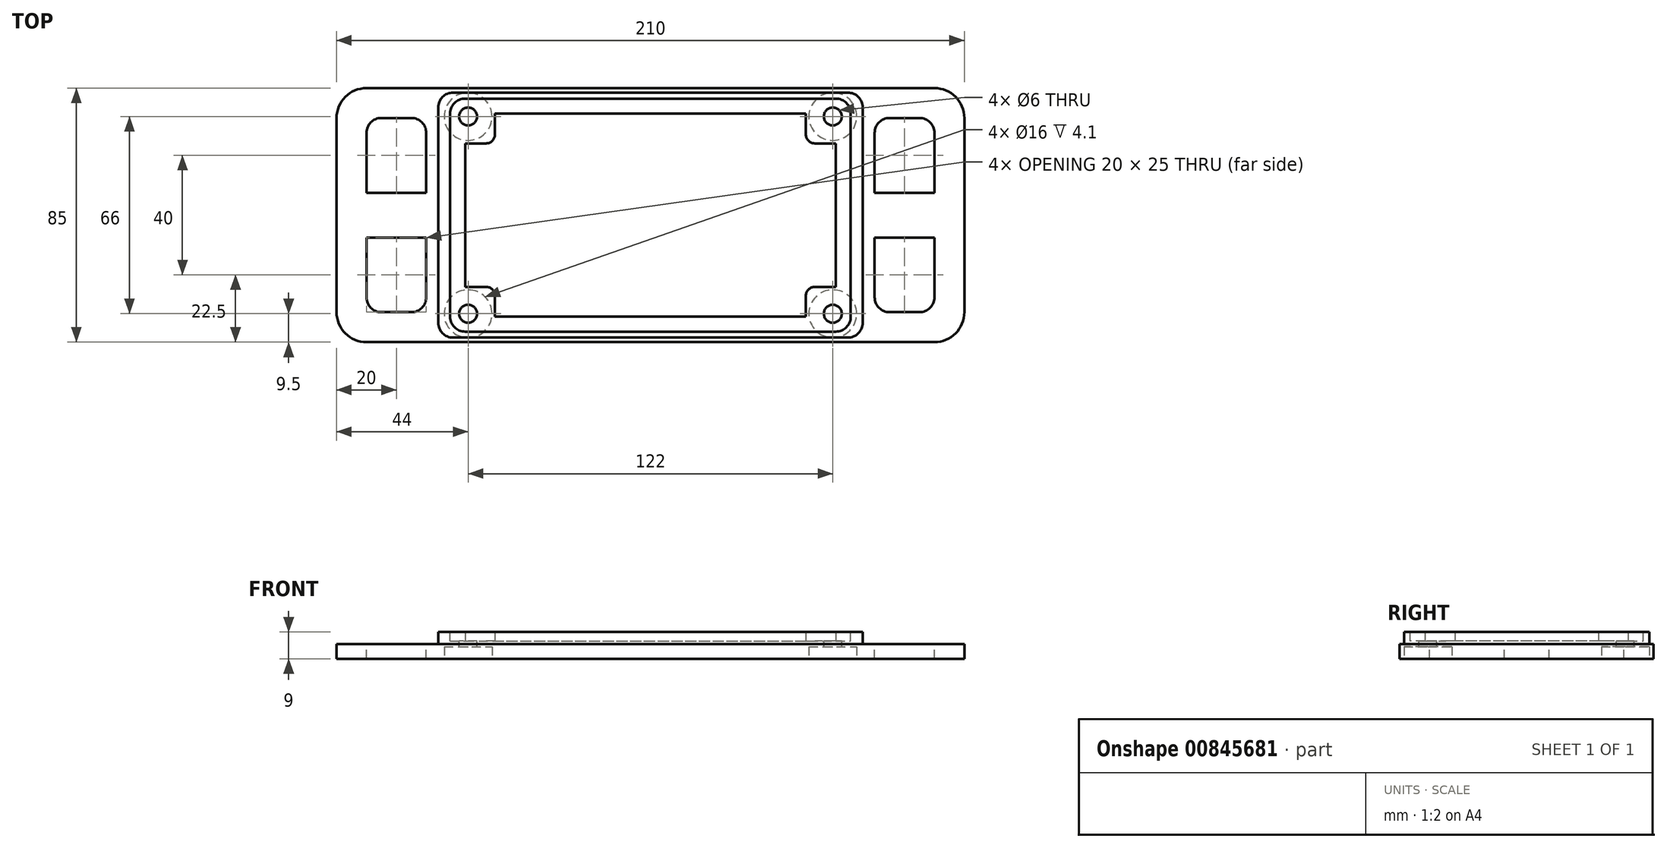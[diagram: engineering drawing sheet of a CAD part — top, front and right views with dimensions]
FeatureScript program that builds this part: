
annotation { "Feature Type Name" : "Feature", "Feature Type Description" : "" }
export const myFeature = defineFeature(function(context is Context, id is Id, definition is map)
    precondition{}
    {
        {
            var Q0;
            Q0=qCreatedBy(makeId("Top.planeOp"),FACE);
            var sketch = newSketch(context, id + "F0", { "sketchPlane" : qUnion([Q0])});
            skLineSegment(sketch, "E0.bottom", {"start": v(-105, 42.5) * mm, "end": v(105, 42.5) * mm});
            skLineSegment(sketch, "E0.top", {"start": v(-105, -42.5) * mm, "end": v(105, -42.5) * mm});
            skLineSegment(sketch, "E0.left", {"start": v(-105, 42.5) * mm, "end": v(-105, -42.5) * mm});
            skLineSegment(sketch, "E0.right", {"start": v(105, 42.5) * mm, "end": v(105, -42.5) * mm});
            skSolve(sketch);
        }
        {
            var Q0;
            Q0 = qSketchRegion(id + "F0", true);
            extrude(context, id + "F1", {"entities" : qUnion([Q0]), "depth" : 5 * mm, "offsetDistance" : 25 * mm});
        }
        {
            var Q0;
            Q0=makeQuery(id+"F1.opExtrude","SWEPT_EDGE",EDGE,{"disambiguationData":[OSD([sQuery(id+"F0.wireOp",EDGE,"E0.top"),sQuery(id+"F0.wireOp",EDGE,"E0.left")])]});
            var Q1;
            Q1=makeQuery(id+"F1.opExtrude","SWEPT_EDGE",EDGE,{"disambiguationData":[OSD([sQuery(id+"F0.wireOp",EDGE,"E0.bottom"),sQuery(id+"F0.wireOp",EDGE,"E0.left")])]});
            var Q2;
            Q2=makeQuery(id+"F1.opExtrude","SWEPT_EDGE",EDGE,{"disambiguationData":[OSD([sQuery(id+"F0.wireOp",EDGE,"E0.bottom"),sQuery(id+"F0.wireOp",EDGE,"E0.right")])]});
            var Q3;
            Q3=makeQuery(id+"F1.opExtrude","SWEPT_EDGE",EDGE,{"disambiguationData":[OSD([sQuery(id+"F0.wireOp",EDGE,"E0.top"),sQuery(id+"F0.wireOp",EDGE,"E0.right")])]});
            fillet(context, id + "F2", {"entities" : qUnion([Q0, Q1, Q2, Q3]), "radius" : 10 * mm, "tangentPropagation" : true, "allowEdgeOverflow" : false});
        }
        {
            var Q0;
            Q0=makeQuery(id+"F1.opExtrude","CAP_FACE",FACE,{"disambiguationData":[OSD([sQuery(id+"F0.wireOp",EDGE,"E0.bottom"),sQuery(id+"F0.wireOp",EDGE,"E0.top"),sQuery(id+"F0.wireOp",EDGE,"E0.left"),sQuery(id+"F0.wireOp",EDGE,"E0.right")])],"isStart":false});
            var sketch = newSketch(context, id + "F3", { "sketchPlane" : qUnion([Q0])});
            skLineSegment(sketch, "E1.bottom", {"start": v(-66, 41) * mm, "end": v(66, 41) * mm});
            skLineSegment(sketch, "E1.top", {"start": v(-66, -41) * mm, "end": v(66, -41) * mm});
            skLineSegment(sketch, "E1.left", {"start": v(-71, 36) * mm, "end": v(-71, -36) * mm});
            skLineSegment(sketch, "E1.right", {"start": v(71, 36) * mm, "end": v(71, -36) * mm});
            skPoint(sketch, "E2.visualSharp", {"position": v(-71, 41) * mm});
            skArc(sketch, "E2.filletArc", {"start": v(-66, 41) * mm, "mid": v(-69.54, 39.54) * mm, "end": v(-71, 36) * mm});
            skPoint(sketch, "E3.visualSharp", {"position": v(-71, -41) * mm});
            skArc(sketch, "E3.filletArc", {"start": v(-71, -36) * mm, "mid": v(-69.54, -39.54) * mm, "end": v(-66, -41) * mm});
            skPoint(sketch, "E4.visualSharp", {"position": v(71, -41) * mm});
            skArc(sketch, "E4.filletArc", {"start": v(66, -41) * mm, "mid": v(69.54, -39.54) * mm, "end": v(71, -36) * mm});
            skPoint(sketch, "E5.visualSharp", {"position": v(71, 41) * mm});
            skArc(sketch, "E5.filletArc", {"start": v(71, 36) * mm, "mid": v(69.54, 39.54) * mm, "end": v(66, 41) * mm});
            skSolve(sketch);
        }
        {
            var Q0;
            Q0 = qSketchRegion(id + "F3", true);
            extrude(context, id + "F4", {"entities" : qUnion([Q0]), "operationType" : NewBodyOperationType.ADD, "depth" : 4 * mm, "offsetDistance" : 25 * mm});
        }
        {
            var Q0;
            Q0=makeQuery(id+"F4.opExtrude","CAP_FACE",FACE,{"disambiguationData":[OSD([sQuery(id+"F3.wireOp",EDGE,"E1.bottom"),sQuery(id+"F3.wireOp",EDGE,"E1.top"),sQuery(id+"F3.wireOp",EDGE,"E1.left"),sQuery(id+"F3.wireOp",EDGE,"E1.right"),sQuery(id+"F3.wireOp",EDGE,"E2.filletArc"),sQuery(id+"F3.wireOp",EDGE,"E3.filletArc"),sQuery(id+"F3.wireOp",EDGE,"E4.filletArc"),sQuery(id+"F3.wireOp",EDGE,"E5.filletArc")])],"isStart":false});
            var sketch = newSketch(context, id + "F5", { "sketchPlane" : qUnion([Q0])});
            skLineSegment(sketch, "E6.bottom", {"start": v(-62, 39) * mm, "end": v(62, 39) * mm});
            skLineSegment(sketch, "E6.top", {"start": v(-62, -39) * mm, "end": v(62, -39) * mm});
            skLineSegment(sketch, "E6.left", {"start": v(-67, 34) * mm, "end": v(-67, -34) * mm});
            skLineSegment(sketch, "E6.right", {"start": v(67, 34) * mm, "end": v(67, -34) * mm});
            skPoint(sketch, "E7.visualSharp", {"position": v(-67, 39) * mm});
            skArc(sketch, "E7.filletArc", {"start": v(-62, 39) * mm, "mid": v(-65.54, 37.54) * mm, "end": v(-67, 34) * mm});
            skPoint(sketch, "E8.visualSharp", {"position": v(-67, -39) * mm});
            skArc(sketch, "E8.filletArc", {"start": v(-67, -34) * mm, "mid": v(-65.54, -37.54) * mm, "end": v(-62, -39) * mm});
            skPoint(sketch, "E9.visualSharp", {"position": v(67, -39) * mm});
            skArc(sketch, "E9.filletArc", {"start": v(62, -39) * mm, "mid": v(65.54, -37.54) * mm, "end": v(67, -34) * mm});
            skPoint(sketch, "E10.visualSharp", {"position": v(67, 39) * mm});
            skArc(sketch, "E10.filletArc", {"start": v(67, 34) * mm, "mid": v(65.54, 37.54) * mm, "end": v(62, 39) * mm});
            skSolve(sketch);
        }
        {
            var Q0;
            Q0 = qSketchRegion(id + "F5", true);
            extrude(context, id + "F6", {"entities" : qUnion([Q0]), "operationType" : NewBodyOperationType.REMOVE, "oppositeDirection" : true, "depth" : 3 * mm, "offsetDistance" : 25 * mm});
        }
        {
            var Q0;
            Q0=makeQuery(id+"F6.boolean.opBoolean","COPY",FACE,{"derivedFrom":makeQuery(id+"F6.opExtrude","CAP_FACE",FACE,{"disambiguationData":[OSD([sQuery(id+"F5.wireOp",EDGE,"E6.bottom"),sQuery(id+"F5.wireOp",EDGE,"E6.top"),sQuery(id+"F5.wireOp",EDGE,"E6.left"),sQuery(id+"F5.wireOp",EDGE,"E6.right"),sQuery(id+"F5.wireOp",EDGE,"E7.filletArc"),sQuery(id+"F5.wireOp",EDGE,"E8.filletArc"),sQuery(id+"F5.wireOp",EDGE,"E9.filletArc"),sQuery(id+"F5.wireOp",EDGE,"E10.filletArc")])],"isStart":false})});
            var sketch = newSketch(context, id + "F7", { "sketchPlane" : qUnion([Q0])});
            skLineSegment(sketch, "E11.bottom", {"start": v(-52, 34) * mm, "end": v(52, 34) * mm});
            skLineSegment(sketch, "E11.top", {"start": v(-52, -34) * mm, "end": v(52, -34) * mm});
            skLineSegment(sketch, "E11.left", {"start": v(-62, 24) * mm, "end": v(-62, -24) * mm});
            skLineSegment(sketch, "E11.right", {"start": v(62, 24) * mm, "end": v(62, -24) * mm});
            skLineSegment(sketch, "E12.top", {"start": v(-62, 24) * mm, "end": v(-55, 24) * mm});
            skLineSegment(sketch, "E12.right", {"start": v(-52, 34) * mm, "end": v(-52, 27) * mm});
            skPoint(sketch, "E13.visualSharp", {"position": v(-52, 24) * mm});
            skArc(sketch, "E13.filletArc", {"start": v(-55, 24) * mm, "mid": v(-52.88, 24.88) * mm, "end": v(-52, 27) * mm});
            skLineSegment(sketch, "E14", {"start": v(0, 19.7) * mm, "end": v(0, -28.15) * mm, "construction": true});
            skLineSegment(sketch, "E15", {"start": v(-18.01, 0) * mm, "end": v(22.05, 0) * mm, "construction": true});
            skLineSegment(sketch, "E16.MirrorCS", {"start": v(-62, -24) * mm, "end": v(-55, -24) * mm});
            skPoint(sketch, "E17.MirrorP", {"position": v(-52, -24) * mm});
            skArc(sketch, "E18.MirrorCS", {"start": v(-55, -24) * mm, "mid": v(-52.88, -24.88) * mm, "end": v(-52, -27) * mm});
            skLineSegment(sketch, "E19.MirrorCS", {"start": v(-52, -34) * mm, "end": v(-52, -27) * mm});
            skLineSegment(sketch, "E20.MirrorCS", {"start": v(62, 24) * mm, "end": v(55, 24) * mm});
            skArc(sketch, "E21.MirrorCS", {"start": v(55, 24) * mm, "mid": v(52.88, 24.88) * mm, "end": v(52, 27) * mm});
            skLineSegment(sketch, "E22.MirrorCS", {"start": v(52, 34) * mm, "end": v(52, 27) * mm});
            skLineSegment(sketch, "E23.MirrorCS", {"start": v(62, -24) * mm, "end": v(55, -24) * mm});
            skLineSegment(sketch, "E24.MirrorCS", {"start": v(52, -34) * mm, "end": v(52, -27) * mm});
            skArc(sketch, "E25.MirrorCS", {"start": v(55, -24) * mm, "mid": v(52.88, -24.88) * mm, "end": v(52, -27) * mm});
            skPoint(sketch, "E26.orphan", {"position": v(-62, 34) * mm});
            skSolve(sketch);
        }
        {
            var Q0;
            Q0 = qSketchRegion(id + "F7", true);
            extrude(context, id + "F8", {"entities" : qUnion([Q0]), "operationType" : NewBodyOperationType.ADD, "depth" : 3 * mm, "offsetDistance" : 25 * mm});
        }
        {
            var Q0;
            Q0=makeQuery(id+"F6.boolean.opBoolean","COPY",FACE,{"derivedFrom":makeQuery(id+"F6.opExtrude","CAP_FACE",FACE,{"disambiguationData":[OSD([sQuery(id+"F5.wireOp",EDGE,"E6.bottom"),sQuery(id+"F5.wireOp",EDGE,"E6.top"),sQuery(id+"F5.wireOp",EDGE,"E6.left"),sQuery(id+"F5.wireOp",EDGE,"E6.right"),sQuery(id+"F5.wireOp",EDGE,"E7.filletArc"),sQuery(id+"F5.wireOp",EDGE,"E8.filletArc"),sQuery(id+"F5.wireOp",EDGE,"E9.filletArc"),sQuery(id+"F5.wireOp",EDGE,"E10.filletArc")])],"isStart":false})});
            var sketch = newSketch(context, id + "F9", { "sketchPlane" : qUnion([Q0])});
            skCircle(sketch, "E27", {"center": v(-61, -33) * mm, "radius": 3 * mm});
            skLineSegment(sketch, "E28", {"start": v(0, 18.3) * mm, "end": v(0, -14.07) * mm, "construction": true});
            skLineSegment(sketch, "E29", {"start": v(-30.9, 0) * mm, "end": v(22.99, 0) * mm, "construction": true});
            skCircle(sketch, "E30.MirrorC", {"center": v(-61, 33) * mm, "radius": 3 * mm});
            skCircle(sketch, "E31.MirrorC", {"center": v(61, -33) * mm, "radius": 3 * mm});
            skCircle(sketch, "E32.MirrorC", {"center": v(61, 33) * mm, "radius": 3 * mm});
            skSolve(sketch);
        }
        {
            var Q0;
            Q0 = qSketchRegion(id + "F9", true);
            extrude(context, id + "F10", {"entities" : qUnion([Q0]), "operationType" : NewBodyOperationType.REMOVE, "oppositeDirection" : true, "depth" : 25 * mm, "offsetDistance" : 25 * mm});
        }
        {
            var Q0;
            Q0=makeQuery(id+"F1.opExtrude","CAP_FACE",FACE,{"disambiguationData":[OSD([sQuery(id+"F0.wireOp",EDGE,"E0.bottom"),sQuery(id+"F0.wireOp",EDGE,"E0.top"),sQuery(id+"F0.wireOp",EDGE,"E0.left"),sQuery(id+"F0.wireOp",EDGE,"E0.right")])],"isStart":true});
            var sketch = newSketch(context, id + "F11", { "sketchPlane" : qUnion([Q0])});
            skCircle(sketch, "E33", {"center": v(-61, 33) * mm, "radius": 8 * mm});
            skCircle(sketch, "E34", {"center": v(-61, -33) * mm, "radius": 8 * mm});
            skCircle(sketch, "E35", {"center": v(61, -33) * mm, "radius": 8 * mm});
            skCircle(sketch, "E36", {"center": v(61, 33) * mm, "radius": 8 * mm});
            skSolve(sketch);
        }
        {
            var Q0;
            Q0 = qSketchRegion(id + "F11", true);
            extrude(context, id + "F12", {"entities" : qUnion([Q0]), "operationType" : NewBodyOperationType.REMOVE, "oppositeDirection" : true, "depth" : 4.1 * mm, "offsetDistance" : 25 * mm});
        }
        {
            var Q0;
            Q0=makeQuery(id+"F1.opExtrude","CAP_FACE",FACE,{"disambiguationData":[OSD([sQuery(id+"F0.wireOp",EDGE,"E0.bottom"),sQuery(id+"F0.wireOp",EDGE,"E0.top"),sQuery(id+"F0.wireOp",EDGE,"E0.left"),sQuery(id+"F0.wireOp",EDGE,"E0.right")])],"isStart":false});
            var sketch = newSketch(context, id + "F13", { "sketchPlane" : qUnion([Q0])});
            skLineSegment(sketch, "E37.bottom", {"start": v(-90, 32.5) * mm, "end": v(-80, 32.5) * mm});
            skLineSegment(sketch, "E37.top", {"start": v(-95, 7.5) * mm, "end": v(-75, 7.5) * mm});
            skLineSegment(sketch, "E37.left", {"start": v(-95, 27.5) * mm, "end": v(-95, 7.5) * mm});
            skLineSegment(sketch, "E37.right", {"start": v(-75, 27.5) * mm, "end": v(-75, 7.5) * mm});
            skLineSegment(sketch, "E38", {"start": v(-27.76, 0) * mm, "end": v(22.14, 0) * mm, "construction": true});
            skLineSegment(sketch, "E39", {"start": v(0, 18.6) * mm, "end": v(0, -20.05) * mm, "construction": true});
            skPoint(sketch, "E40.visualSharp", {"position": v(-95, 32.5) * mm});
            skArc(sketch, "E40.filletArc", {"start": v(-90, 32.5) * mm, "mid": v(-93.54, 31.04) * mm, "end": v(-95, 27.5) * mm});
            skPoint(sketch, "E41.visualSharp", {"position": v(-75, 32.5) * mm});
            skArc(sketch, "E41.filletArc", {"start": v(-75, 27.5) * mm, "mid": v(-76.46, 31.04) * mm, "end": v(-80, 32.5) * mm});
            skLineSegment(sketch, "E42.MirrorCS", {"start": v(-75, -27.5) * mm, "end": v(-75, -7.5) * mm});
            skArc(sketch, "E43.MirrorCS", {"start": v(-75, -27.5) * mm, "mid": v(-76.46, -31.04) * mm, "end": v(-80, -32.5) * mm});
            skLineSegment(sketch, "E44.MirrorCS", {"start": v(-90, -32.5) * mm, "end": v(-80, -32.5) * mm});
            skArc(sketch, "E45.MirrorCS", {"start": v(-90, -32.5) * mm, "mid": v(-93.54, -31.04) * mm, "end": v(-95, -27.5) * mm});
            skLineSegment(sketch, "E46.MirrorCS", {"start": v(-95, -7.5) * mm, "end": v(-75, -7.5) * mm});
            skLineSegment(sketch, "E47.MirrorCS", {"start": v(-95, -27.5) * mm, "end": v(-95, -7.5) * mm});
            skArc(sketch, "E48.MirrorCS", {"start": v(75, 27.5) * mm, "mid": v(76.46, 31.04) * mm, "end": v(80, 32.5) * mm});
            skLineSegment(sketch, "E49.MirrorCS", {"start": v(90, 32.5) * mm, "end": v(80, 32.5) * mm});
            skArc(sketch, "E50.MirrorCS", {"start": v(90, 32.5) * mm, "mid": v(93.54, 31.04) * mm, "end": v(95, 27.5) * mm});
            skArc(sketch, "E51.MirrorCS", {"start": v(75, -27.5) * mm, "mid": v(76.46, -31.04) * mm, "end": v(80, -32.5) * mm});
            skLineSegment(sketch, "E52.MirrorCS", {"start": v(90, -32.5) * mm, "end": v(80, -32.5) * mm});
            skArc(sketch, "E53.MirrorCS", {"start": v(90, -32.5) * mm, "mid": v(93.54, -31.04) * mm, "end": v(95, -27.5) * mm});
            skLineSegment(sketch, "E54.MirrorCS", {"start": v(95, -27.5) * mm, "end": v(95, -7.5) * mm});
            skLineSegment(sketch, "E55.MirrorCS", {"start": v(75, -27.5) * mm, "end": v(75, -7.5) * mm});
            skLineSegment(sketch, "E56.MirrorCS", {"start": v(75, 27.5) * mm, "end": v(75, 7.5) * mm});
            skLineSegment(sketch, "E57.MirrorCS", {"start": v(95, 27.5) * mm, "end": v(95, 7.5) * mm});
            skLineSegment(sketch, "E58.MirrorCS", {"start": v(95, -7.5) * mm, "end": v(75, -7.5) * mm});
            skLineSegment(sketch, "E59.MirrorCS", {"start": v(95, 7.5) * mm, "end": v(75, 7.5) * mm});
            skSolve(sketch);
        }
        {
            var Q0;
            Q0 = qSketchRegion(id + "F13", true);
            extrude(context, id + "F14", {"entities" : qUnion([Q0]), "operationType" : NewBodyOperationType.REMOVE, "oppositeDirection" : true, "depth" : 25 * mm, "offsetDistance" : 25 * mm});
        }
    });
